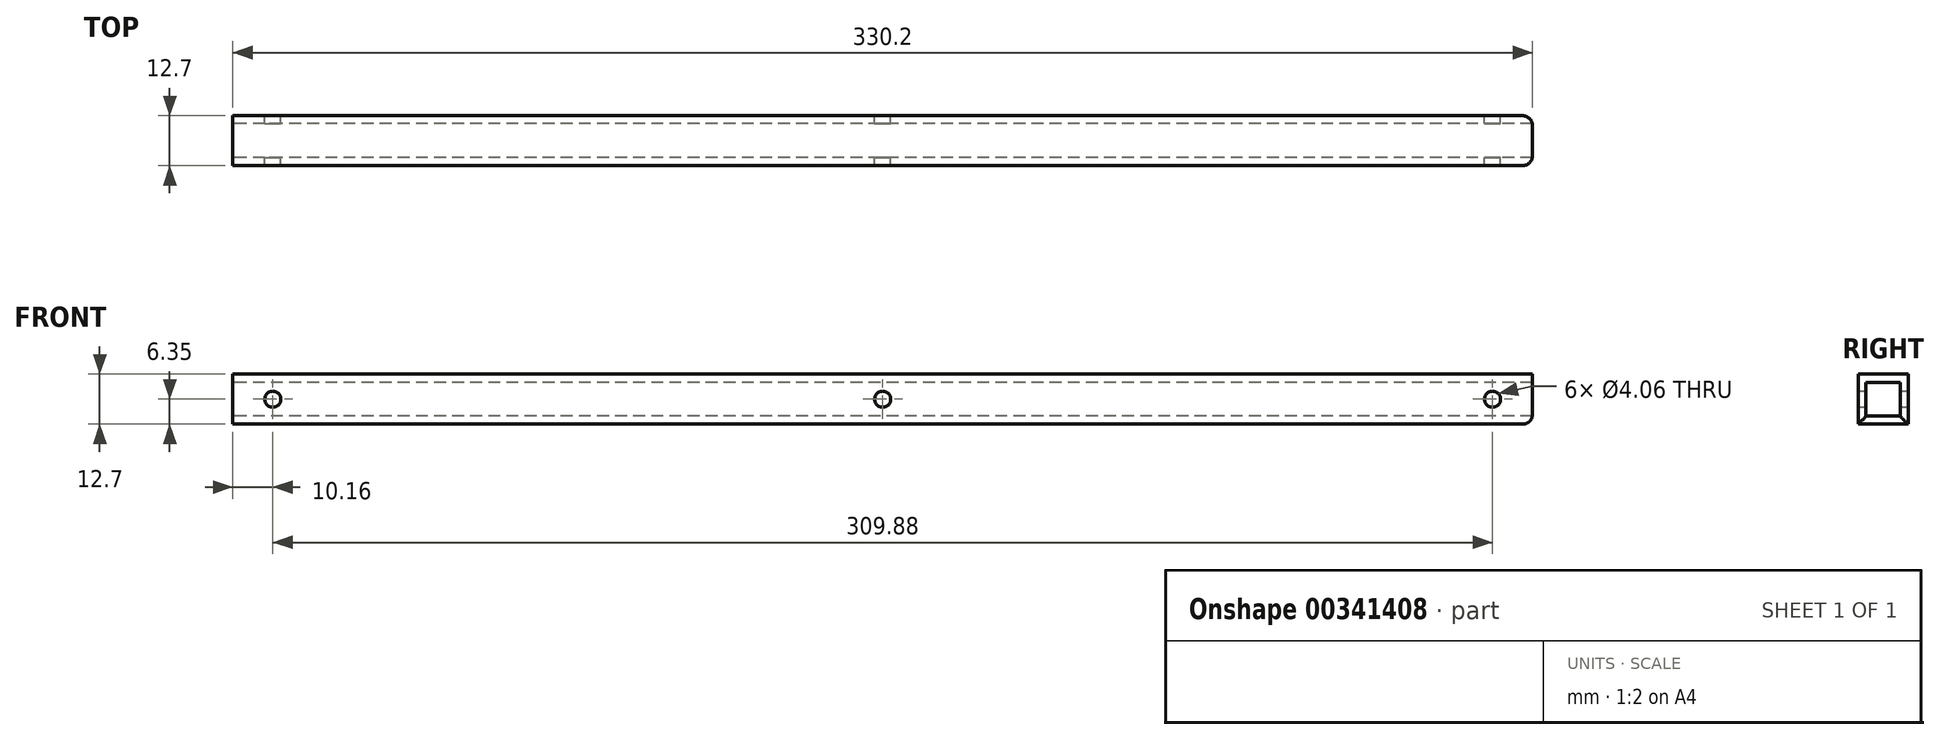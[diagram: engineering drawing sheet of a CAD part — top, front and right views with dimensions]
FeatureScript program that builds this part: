
annotation { "Feature Type Name" : "Feature", "Feature Type Description" : "" }
export const myFeature = defineFeature(function(context is Context, id is Id, definition is map)
    precondition{}
    {
        {
            var Q0;
            Q0=qCreatedBy(makeId("Front.planeOp"),FACE);
            var sketch = newSketch(context, id + "F0", { "sketchPlane" : qUnion([Q0])});
            skLineSegment(sketch, "E0.bottom", {"start": v(165.1, -6.35) * mm, "end": v(-165.1, -6.35) * mm});
            skLineSegment(sketch, "E0.top", {"start": v(165.1, 6.35) * mm, "end": v(-165.1, 6.35) * mm});
            skLineSegment(sketch, "E0.left", {"start": v(165.1, -6.35) * mm, "end": v(165.1, 6.35) * mm});
            skLineSegment(sketch, "E0.right", {"start": v(-165.1, -6.35) * mm, "end": v(-165.1, 6.35) * mm});
            skPoint(sketch, "E0.middle", {"position": v(0, 0) * mm});
            skCircle(sketch, "E1", {"center": v(-154.94, 0) * mm, "radius": 2.03 * mm});
            skCircle(sketch, "E2", {"center": v(154.94, 0) * mm, "radius": 2.03 * mm});
            skCircle(sketch, "E3", {"center": v(0, 0) * mm, "radius": 2.03 * mm});
            skSolve(sketch);
        }
        {
            var Q0;
            Q0=makeQuery(id+"F0.imprint","IMPRINT",FACE,{"disambiguationData":[TD([[makeQuery(id+"F0.imprint","IMPRINT",EDGE,{"derivedFrom":sQuery(id+"F0.wireOp",EDGE,"E0.bottom")}),-1.0]])]});
            extrude(context, id + "F1", {"entities" : qUnion([Q0]), "depth" : 12.7 * mm, "symmetric" : true});
        }
        {
            var Q0;
            Q0=makeQuery(id+"F1.opExtrude","SWEPT_EDGE",EDGE,{"disambiguationData":[OSD([sQuery(id+"F0.wireOp",EDGE,"E0.bottom"),sQuery(id+"F0.wireOp",EDGE,"E0.left")])]});
            var Q1;
            Q1=makeQuery(id+"F1.opExtrude","CAP_EDGE",EDGE,{"disambiguationData":[OSD([sQuery(id+"F0.wireOp",EDGE,"E0.left")])],"isStart":true});
            var Q2;
            Q2=makeQuery(id+"F1.opExtrude","CAP_EDGE",EDGE,{"disambiguationData":[OSD([sQuery(id+"F0.wireOp",EDGE,"E0.left")])],"isStart":false});
            fillet(context, id + "F2", {"entities" : qUnion([Q0, Q1, Q2]), "radius" : 2.54 * mm, "tangentPropagation" : true, "allowEdgeOverflow" : false});
        }
        {
            var Q0;
            Q0=makeQuery(id+"F1.opExtrude","SWEPT_FACE",FACE,{"disambiguationData":[OSD([sQuery(id+"F0.wireOp",EDGE,"E0.right")])]});
            var sketch = newSketch(context, id + "F3", { "sketchPlane" : qUnion([Q0])});
            skLineSegment(sketch, "E4.bottom", {"start": v(4.33, -4.22) * mm, "end": v(-4.33, -4.22) * mm});
            skLineSegment(sketch, "E4.top", {"start": v(4.33, 4.22) * mm, "end": v(-4.33, 4.22) * mm});
            skLineSegment(sketch, "E4.left", {"start": v(4.33, -4.22) * mm, "end": v(4.33, 4.22) * mm});
            skLineSegment(sketch, "E4.right", {"start": v(-4.33, -4.22) * mm, "end": v(-4.33, 4.22) * mm});
            skPoint(sketch, "E4.middle", {"position": v(0, 0) * mm});
            skSolve(sketch);
        }
        {
            var Q0;
            Q0=makeQuery(id+"F3.imprint","IMPRINT",FACE,{"disambiguationData":[TD([[makeQuery(id+"F3.imprint","IMPRINT",EDGE,{"derivedFrom":sQuery(id+"F3.wireOp",EDGE,"E4.bottom")}),-1.0]])]});
            extrude(context, id + "F4", {"entities" : qUnion([Q0]), "operationType" : NewBodyOperationType.REMOVE, "oppositeDirection" : true, "depth" : 330.2 * mm});
        }
    });
